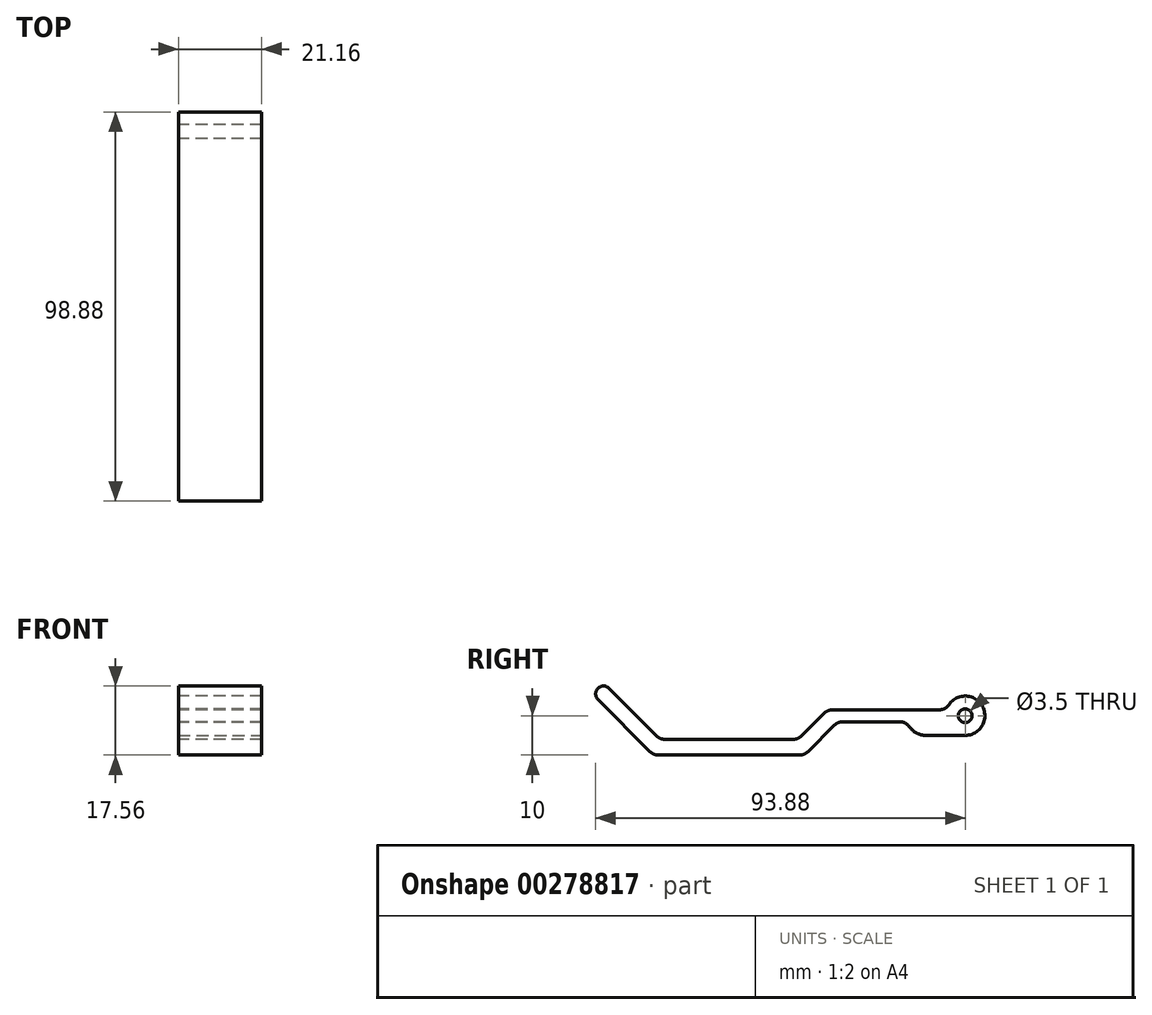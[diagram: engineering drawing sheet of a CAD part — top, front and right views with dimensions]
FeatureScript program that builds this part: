
annotation { "Feature Type Name" : "Feature", "Feature Type Description" : "" }
export const myFeature = defineFeature(function(context is Context, id is Id, definition is map)
    precondition{}
    {
        {
            var Q0;
            Q0=qCreatedBy(makeId("Right.planeOp"),FACE);
            var sketch = newSketch(context, id + "F0", { "sketchPlane" : qUnion([Q0])});
            skCircle(sketch, "E0", {"center": v(0, 0) * mm, "radius": 1.75 * mm});
            skLineSegment(sketch, "E1", {"start": v(0, 0) * mm, "end": v(-10, 0) * mm, "construction": true});
            skLineSegment(sketch, "E2", {"start": v(-10, 0) * mm, "end": v(-60, 0) * mm, "construction": true});
            skPoint(sketch, "E3", {"position": v(-42.5, 0) * mm});
            skLineSegment(sketch, "E4", {"start": v(-60, 0) * mm, "end": v(-60, 34.1) * mm, "construction": true});
            skCircle(sketch, "E5", {"center": v(-10, 0) * mm, "radius": 5 * mm, "construction": true});
            skArc(sketch, "E6", {"start": v(-4.77, -1.5) * mm, "mid": v(5, 0) * mm, "end": v(-4.77, 1.5) * mm});
            skLineSegment(sketch, "E7", {"start": v(-4.77, 1.5) * mm, "end": v(-35, 1.5) * mm});
            skLineSegment(sketch, "E8", {"start": v(-4.77, -1.5) * mm, "end": v(-5.23, -1.5) * mm});
            skArc(sketch, "E9", {"start": v(-5.23, -1.5) * mm, "mid": v(-10, -5) * mm, "end": v(-14.77, -1.5) * mm});
            skLineSegment(sketch, "E10", {"start": v(-77.5, -6) * mm, "end": v(-42.5, -6) * mm});
            skPoint(sketch, "E11", {"position": v(-60, -6) * mm});
            skLineSegment(sketch, "E12", {"start": v(-35, 1.5) * mm, "end": v(-42.5, -6) * mm});
            skLineSegment(sketch, "E13", {"start": v(-14.77, -1.5) * mm, "end": v(-32.34, -1.5) * mm});
            skLineSegment(sketch, "E14", {"start": v(-32.34, -1.5) * mm, "end": v(-40.84, -10) * mm});
            skLineSegment(sketch, "E15", {"start": v(-40.84, -10) * mm, "end": v(-79.16, -10) * mm});
            skLineSegment(sketch, "E16", {"start": v(-77.5, -6) * mm, "end": v(-90.47, 6.97) * mm});
            skLineSegment(sketch, "E17", {"start": v(-79.16, -10) * mm, "end": v(-93.3, 4.14) * mm});
            skArc(sketch, "E18", {"start": v(-90.47, 6.97) * mm, "mid": v(-93.3, 6.97) * mm, "end": v(-93.3, 4.14) * mm});
            skSolve(sketch);
        }
        {
            var Q0;
            Q0=qSketchRegion(id+"F0",true);
            extrude(context, id + "F1", {"entities" : qUnion([Q0]), "endBound" : BoundingType.SYMMETRIC, "depth" : 31.75 * mm});
        }
        {
            var Q0;
            Q0=makeQuery(id+"F1.opExtrude","CAP_FACE",FACE,{"disambiguationData":[OSD([sQuery(id+"F0.wireOp",EDGE,"E0"),sQuery(id+"F0.wireOp",EDGE,"E6"),sQuery(id+"F0.wireOp",EDGE,"E7"),sQuery(id+"F0.wireOp",EDGE,"E8"),sQuery(id+"F0.wireOp",EDGE,"E9"),sQuery(id+"F0.wireOp",EDGE,"E10"),sQuery(id+"F0.wireOp",EDGE,"E12"),sQuery(id+"F0.wireOp",EDGE,"E13"),sQuery(id+"F0.wireOp",EDGE,"E14"),sQuery(id+"F0.wireOp",EDGE,"E15"),sQuery(id+"F0.wireOp",EDGE,"E16"),sQuery(id+"F0.wireOp",EDGE,"E17"),sQuery(id+"F0.wireOp",EDGE,"E18")])],"isStart":false});
            var sketch = newSketch(context, id + "F2", { "sketchPlane" : qUnion([Q0])});
            skLineSegment(sketch, "E19", {"start": v(-10, -5) * mm, "end": v(0, -5) * mm});
            skArc(sketch, "E20.0", {"start": v(-5.23, -1.5) * mm, "mid": v(-7.04, -4.03) * mm, "end": v(-10, -5) * mm});
            skArc(sketch, "E20.1", {"start": v(-4.77, -1.5) * mm, "mid": v(-2.96, -4.03) * mm, "end": v(0, -5) * mm});
            skLineSegment(sketch, "E20.2", {"start": v(-4.77, -1.5) * mm, "end": v(-5.23, -1.5) * mm});
            skPoint(sketch, "E21.orphan", {"position": v(-14.77, -1.5) * mm});
            skPoint(sketch, "E22.orphan", {"position": v(-4.77, 1.5) * mm});
            skSolve(sketch);
        }
        {
            var Q0;
            Q0=qSketchRegion(id+"F2",true);
            var Q1;
            Q1=makeQuery(id+"F1.opExtrude","CAP_FACE",FACE,{"disambiguationData":[OSD([sQuery(id+"F0.wireOp",EDGE,"E0"),sQuery(id+"F0.wireOp",EDGE,"E6"),sQuery(id+"F0.wireOp",EDGE,"E7"),sQuery(id+"F0.wireOp",EDGE,"E8"),sQuery(id+"F0.wireOp",EDGE,"E9"),sQuery(id+"F0.wireOp",EDGE,"E10"),sQuery(id+"F0.wireOp",EDGE,"E12"),sQuery(id+"F0.wireOp",EDGE,"E13"),sQuery(id+"F0.wireOp",EDGE,"E14"),sQuery(id+"F0.wireOp",EDGE,"E15"),sQuery(id+"F0.wireOp",EDGE,"E16"),sQuery(id+"F0.wireOp",EDGE,"E17"),sQuery(id+"F0.wireOp",EDGE,"E18")])],"isStart":true});
            extrude(context, id + "F3", {"entities" : qUnion([Q0]), "operationType" : NewBodyOperationType.ADD, "endBound" : BoundingType.UP_TO_SURFACE, "oppositeDirection" : true, "endBoundEntityFace" : qUnion([Q1]), "depth" : 25 * mm});
        }
        {
            var Q0;
            Q0=makeQuery(id+"F1.opExtrude","SWEPT_EDGE",EDGE,{"disambiguationData":[OSD([sQuery(id+"F0.wireOp",EDGE,"E6"),sQuery(id+"F0.wireOp",EDGE,"E7")])]});
            var Q1;
            Q1=makeQuery(id+"F1.opExtrude","SWEPT_EDGE",EDGE,{"disambiguationData":[OSD([sQuery(id+"F0.wireOp",EDGE,"E9"),sQuery(id+"F0.wireOp",EDGE,"E13")])]});
            var Q2;
            Q2=makeQuery(id+"F1.opExtrude","SWEPT_EDGE",EDGE,{"disambiguationData":[OSD([sQuery(id+"F0.wireOp",EDGE,"E10"),sQuery(id+"F0.wireOp",EDGE,"E16")])]});
            var Q3;
            Q3=makeQuery(id+"F1.opExtrude","SWEPT_EDGE",EDGE,{"disambiguationData":[OSD([sQuery(id+"F0.wireOp",EDGE,"E15"),sQuery(id+"F0.wireOp",EDGE,"E17")])]});
            var Q4;
            Q4=makeQuery(id+"F1.opExtrude","SWEPT_EDGE",EDGE,{"disambiguationData":[OSD([sQuery(id+"F0.wireOp",EDGE,"E14"),sQuery(id+"F0.wireOp",EDGE,"E15")])]});
            var Q5;
            Q5=makeQuery(id+"F1.opExtrude","SWEPT_EDGE",EDGE,{"disambiguationData":[OSD([sQuery(id+"F0.wireOp",EDGE,"E13"),sQuery(id+"F0.wireOp",EDGE,"E14")])]});
            var Q6;
            Q6=makeQuery(id+"F1.opExtrude","SWEPT_EDGE",EDGE,{"disambiguationData":[OSD([sQuery(id+"F0.wireOp",EDGE,"E10"),sQuery(id+"F0.wireOp",EDGE,"E12")])]});
            var Q7;
            Q7=makeQuery(id+"F1.opExtrude","SWEPT_EDGE",EDGE,{"disambiguationData":[OSD([sQuery(id+"F0.wireOp",EDGE,"E7"),sQuery(id+"F0.wireOp",EDGE,"E12")])]});
            fillet(context, id + "F4", {"entities" : qUnion([Q0, Q1, Q2, Q3, Q4, Q5, Q6, Q7]), "radius" : 3 * mm, "tangentPropagation" : true, "allowEdgeOverflow" : false});
        }
        {
            var Q0;
            Q0=qCreatedBy(makeId("Top.planeOp"),FACE);
            var sketch = newSketch(context, id + "F5", { "sketchPlane" : qUnion([Q0])});
            skLineSegment(sketch, "E23", {"start": v(0, 0) * mm, "end": v(0, -50.55) * mm, "construction": true});
            skLineSegment(sketch, "E24.0", {"start": v(15.88, -10) * mm, "end": v(15.88, 0) * mm, "construction": true});
            skPoint(sketch, "E25", {"position": v(0, -15) * mm});
            skPoint(sketch, "E26", {"position": v(0, -20) * mm});
            skLineSegment(sketch, "E27.0", {"start": v(-15.88, 5) * mm, "end": v(-15.88, -4.13) * mm, "construction": true});
            skLineSegment(sketch, "E28.bottom", {"start": v(-15.88, 5) * mm, "end": v(-10.87, 5) * mm});
            skLineSegment(sketch, "E28.top", {"start": v(-15.88, -30) * mm, "end": v(-10.87, -30) * mm});
            skLineSegment(sketch, "E28.left", {"start": v(-15.88, 5) * mm, "end": v(-15.88, -30) * mm});
            skLineSegment(sketch, "E28.right", {"start": v(-10.87, 5) * mm, "end": v(-10.87, -30) * mm});
            skLineSegment(sketch, "E29.MirrorCS", {"start": v(15.88, -30) * mm, "end": v(10.87, -30) * mm});
            skLineSegment(sketch, "E30.MirrorCS", {"start": v(10.87, 5) * mm, "end": v(10.87, -30) * mm});
            skLineSegment(sketch, "E31.MirrorCS", {"start": v(15.88, 5) * mm, "end": v(15.88, -30) * mm});
            skLineSegment(sketch, "E32.MirrorCS", {"start": v(15.88, 5) * mm, "end": v(10.87, 5) * mm});
            skSolve(sketch);
        }
        {
            var Q0;
            Q0=qSketchRegion(id+"F5",true);
            extrude(context, id + "F6", {"entities" : qUnion([Q0]), "operationType" : NewBodyOperationType.REMOVE, "endBound" : BoundingType.THROUGH_ALL, "oppositeDirection" : true, "depth" : 25 * mm, "hasSecondDirection" : true, "secondDirectionBound" : SecondDirectionBoundingType.THROUGH_ALL, "secondDirectionOppositeDirection" : false, "secondDirectionDepth" : 25 * mm});
        }
        {
            var Q0;
            Q0=makeQuery(id+"F6.boolean.opBoolean","INTERSECT",EDGE,{"derivedFrom":[makeQuery(id+"F1.opExtrude","SWEPT_FACE",FACE,{"disambiguationData":[OSD([sQuery(id+"F0.wireOp",EDGE,"E13")])]}),makeQuery(id+"F6.opExtrude","SWEPT_FACE",FACE,{"disambiguationData":[OSD([sQuery(id+"F5.wireOp",EDGE,"E29.MirrorCS")])]})]});
            var Q1;
            Q1=makeQuery(id+"F6.boolean.opBoolean","INTERSECT",EDGE,{"derivedFrom":[makeQuery(id+"F1.opExtrude","SWEPT_FACE",FACE,{"disambiguationData":[OSD([sQuery(id+"F0.wireOp",EDGE,"E7")])]}),makeQuery(id+"F6.opExtrude","SWEPT_FACE",FACE,{"disambiguationData":[OSD([sQuery(id+"F5.wireOp",EDGE,"E29.MirrorCS")])]})]});
            var Q2;
            Q2=makeQuery(id+"F6.boolean.opBoolean","INTERSECT",EDGE,{"derivedFrom":[makeQuery(id+"F1.opExtrude","SWEPT_FACE",FACE,{"disambiguationData":[OSD([sQuery(id+"F0.wireOp",EDGE,"E7")])]}),makeQuery(id+"F6.opExtrude","SWEPT_FACE",FACE,{"disambiguationData":[OSD([sQuery(id+"F5.wireOp",EDGE,"E28.top")])]})]});
            var Q3;
            Q3=makeQuery(id+"F6.boolean.opBoolean","INTERSECT",EDGE,{"derivedFrom":[makeQuery(id+"F1.opExtrude","SWEPT_FACE",FACE,{"disambiguationData":[OSD([sQuery(id+"F0.wireOp",EDGE,"E13")])]}),makeQuery(id+"F6.opExtrude","SWEPT_FACE",FACE,{"disambiguationData":[OSD([sQuery(id+"F5.wireOp",EDGE,"E28.top")])]})]});
            fillet(context, id + "F7", {"entities" : qUnion([Q0, Q1, Q2, Q3]), "radius" : 1.5 * mm, "tangentPropagation" : true, "allowEdgeOverflow" : false});
        }
        {
            var Q0;
            Q0=makeQuery(id+"F6.boolean.opBoolean","COPY",FACE,{"derivedFrom":makeQuery(id+"F6.opExtrude","SWEPT_FACE",FACE,{"disambiguationData":[OSD([sQuery(id+"F5.wireOp",EDGE,"E30.MirrorCS")])]})});
            extrude(context, id + "F8", {"entities" : qUnion([Q0]), "operationType" : NewBodyOperationType.REMOVE, "oppositeDirection" : true, "depth" : 0.3 * mm});
        }
        {
            var Q0;
            Q0=makeQuery(id+"F6.boolean.opBoolean","COPY",FACE,{"derivedFrom":makeQuery(id+"F6.opExtrude","SWEPT_FACE",FACE,{"disambiguationData":[OSD([sQuery(id+"F5.wireOp",EDGE,"E28.right")])]})});
            extrude(context, id + "F9", {"entities" : qUnion([Q0]), "operationType" : NewBodyOperationType.REMOVE, "oppositeDirection" : true, "depth" : 0.3 * mm});
        }
        {
            var Q0;
            Q0=makeQuery(id+"F3.boolean.opBoolean","MERGE",FACE,{"derivedFrom":[makeQuery(id+"F1.opExtrude","CAP_FACE",FACE,{"disambiguationData":[OSD([sQuery(id+"F0.wireOp",EDGE,"E0"),sQuery(id+"F0.wireOp",EDGE,"E6"),sQuery(id+"F0.wireOp",EDGE,"E7"),sQuery(id+"F0.wireOp",EDGE,"E8"),sQuery(id+"F0.wireOp",EDGE,"E9"),sQuery(id+"F0.wireOp",EDGE,"E10"),sQuery(id+"F0.wireOp",EDGE,"E12"),sQuery(id+"F0.wireOp",EDGE,"E13"),sQuery(id+"F0.wireOp",EDGE,"E14"),sQuery(id+"F0.wireOp",EDGE,"E15"),sQuery(id+"F0.wireOp",EDGE,"E16"),sQuery(id+"F0.wireOp",EDGE,"E17"),sQuery(id+"F0.wireOp",EDGE,"E18")])],"isStart":false}),makeQuery(id+"F3.opExtrude","CAP_FACE",FACE,{"disambiguationData":[OSD([sQuery(id+"F2.wireOp",EDGE,"E19"),sQuery(id+"F2.wireOp",EDGE,"E20.0"),sQuery(id+"F2.wireOp",EDGE,"E20.1"),sQuery(id+"F2.wireOp",EDGE,"E20.2")])],"isStart":true})]});
            var Q1;
            Q1=makeQuery(id+"F8.boolean.opBoolean","COPY",FACE,{"derivedFrom":makeQuery(id+"F8.opExtrude","CAP_FACE",FACE,{"disambiguationData":[OSD([sQuery(id+"F5.wireOp",EDGE,"E30.MirrorCS")])],"isStart":false})});
            extrude(context, id + "F10", {"entities" : qUnion([Q0]), "operationType" : NewBodyOperationType.REMOVE, "endBound" : BoundingType.UP_TO_SURFACE, "oppositeDirection" : true, "endBoundEntityFace" : qUnion([Q1]), "depth" : 25 * mm});
        }
        {
            var Q0;
            {var subQ0=sQuery(id+"F0.wireOp",EDGE,"E18");var subQ1=sQuery(id+"F0.wireOp",EDGE,"E17");var subQ2=sQuery(id+"F0.wireOp",EDGE,"E16");var subQ3=sQuery(id+"F0.wireOp",EDGE,"E15");var subQ4=sQuery(id+"F0.wireOp",EDGE,"E14");var subQ5=sQuery(id+"F0.wireOp",EDGE,"E13");var subQ6=sQuery(id+"F0.wireOp",EDGE,"E12");var subQ7=sQuery(id+"F0.wireOp",EDGE,"E10");var subQ8=sQuery(id+"F0.wireOp",EDGE,"E9");var subQ9=sQuery(id+"F0.wireOp",EDGE,"E8");var subQ10=sQuery(id+"F0.wireOp",EDGE,"E7");var subQ11=sQuery(id+"F0.wireOp",EDGE,"E6");var subQ12=sQuery(id+"F0.wireOp",EDGE,"E0");Q0=makeQuery(id+"F3.boolean.opBoolean","MERGE",FACE,{"derivedFrom":[makeQuery(id+"F1.opExtrude","CAP_FACE",FACE,{"disambiguationData":[OSD([subQ12,subQ11,subQ10,subQ9,subQ8,subQ7,subQ6,subQ5,subQ4,subQ3,subQ2,subQ1,subQ0])],"isStart":true}),makeQuery(id+"F3.opExtrude","CAP_FACE",FACE,{"disambiguationData":[OSD([subQ12,subQ11,subQ10,subQ9,subQ8,subQ7,subQ6,subQ5,subQ4,subQ3,subQ2,subQ1,subQ0])],"isStart":false})]});}
            var Q1;
            Q1=makeQuery(id+"F9.boolean.opBoolean","COPY",FACE,{"derivedFrom":makeQuery(id+"F9.opExtrude","CAP_FACE",FACE,{"disambiguationData":[OSD([sQuery(id+"F5.wireOp",EDGE,"E28.right")])],"isStart":false})});
            extrude(context, id + "F11", {"entities" : qUnion([Q0]), "operationType" : NewBodyOperationType.REMOVE, "endBound" : BoundingType.UP_TO_SURFACE, "oppositeDirection" : true, "endBoundEntityFace" : qUnion([Q1]), "depth" : 25 * mm});
        }
    });
